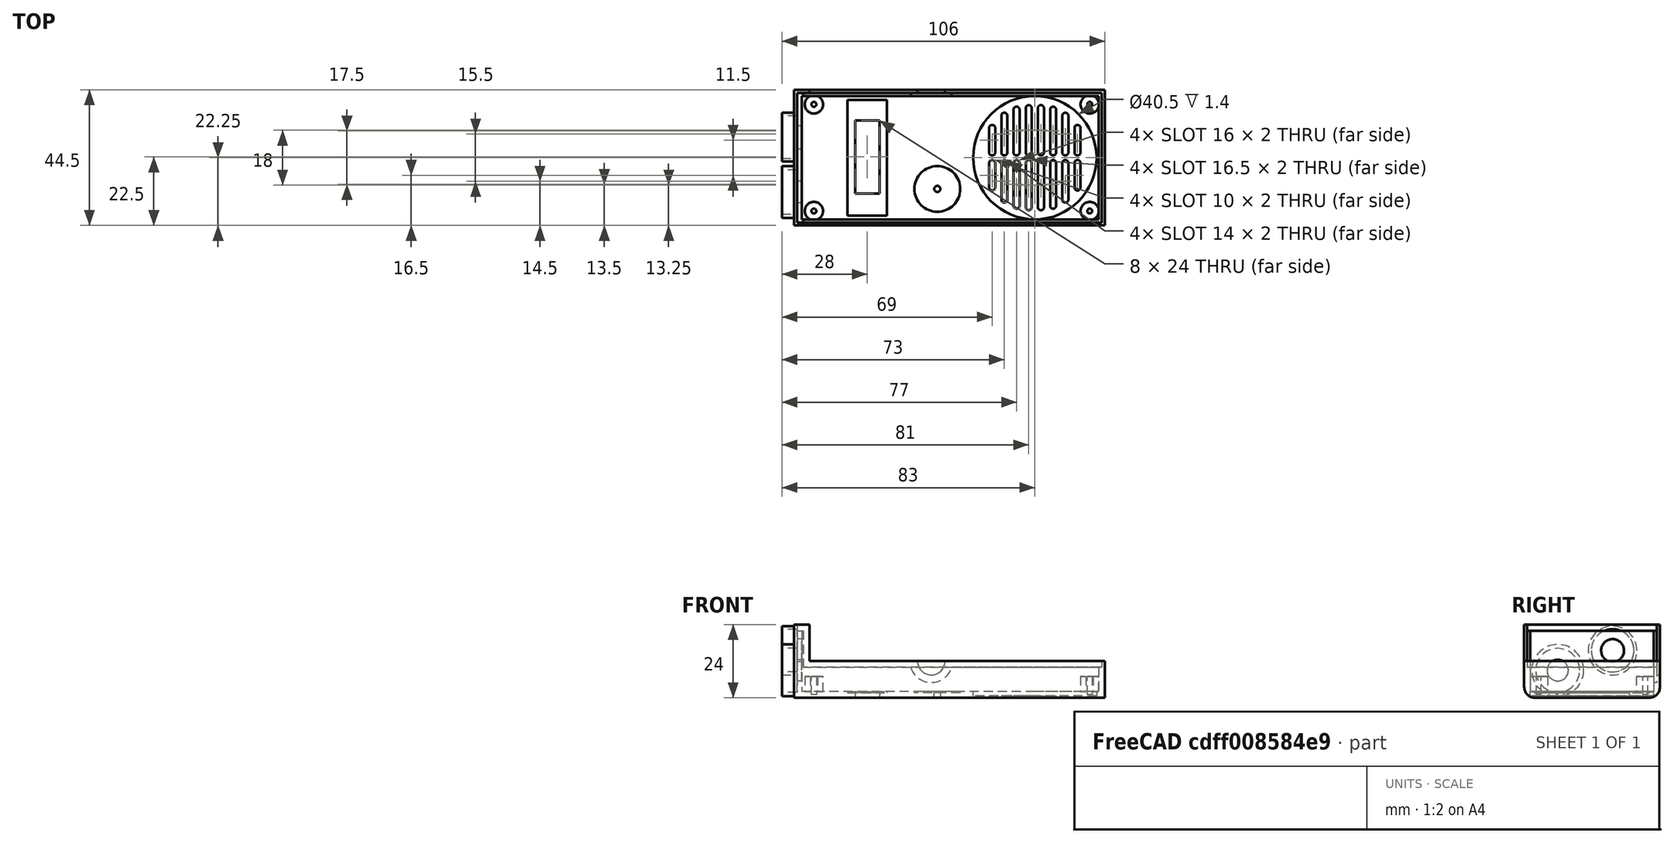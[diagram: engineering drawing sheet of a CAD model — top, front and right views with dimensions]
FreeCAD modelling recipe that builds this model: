
FCSTD DOCUMENT  (FreeCAD 0.20R)
Label: base
License: All rights reserved
LicenseURL: http://en.wikipedia.org/wiki/All_rights_reserved
objects: Sketcher::SketchObject×17, PartDesign::Pocket×14, PartDesign::Pad×3, PartDesign::Plane×2, PartDesign::Mirrored×2, PartDesign::Fillet×1, PartDesign::MultiTransform×1, PartDesign::Body×1
note: 59 computed .brp shape members not serialized (recipe doc carries the construction recipe); baked Part::Feature solids carry a one-line shape summary decoded from their .brp

FEATURE [Sketcher::SketchObject] Sketch  label="sketch_foundation"
  FullyConstrained = true
  MapMode = 5
  Support = -> [XY_Plane]
  sketch-geometry (4):
    g0: LineSegment StartX=0 StartY=0 StartZ=0 EndX=102 EndY=0 EndZ=0
    g1: LineSegment StartX=102 StartY=0 StartZ=0 EndX=102 EndY=44.5 EndZ=0
    g2: LineSegment StartX=102 StartY=44.5 StartZ=0 EndX=0 EndY=44.5 EndZ=0
    g3: LineSegment StartX=0 StartY=44.5 StartZ=0 EndX=0 EndY=0 EndZ=0
  constraints (11):
    c: Coincident(g0,g1)
    c: Coincident(g1,g2)
    c: Coincident(g2,g3)
    c: Coincident(g3,g0)
    c: Horizontal(g0)
    c: Horizontal(g2)
    c: Vertical(g1)
    c: Vertical(g3)
    c: Coincident(g0,g-1)
    c: Distance(g3) = 44.5
    c: Distance(g2) = 102
FEATURE [PartDesign::Pad] Pad  label="pad_foundation"
  Direction = (0,0,1)
  Length = 24
  Length2 = 10
  Profile = -> Sketch
  ReferenceAxis = -> Sketch [N_Axis]
  Type = 0
FEATURE [Sketcher::SketchObject] Sketch001  label="sketch_pocket_foundation"
  FullyConstrained = true
  MapMode = 5
  Placement = pos=(0,0,24) rot=(0,0,1;0rad)
  Support = -> [Pad]
  sketch-geometry (4):
    g0: LineSegment StartX=2.5 StartY=42.5 StartZ=0 EndX=100 EndY=42.5 EndZ=0
    g1: LineSegment StartX=100 StartY=42.5 StartZ=0 EndX=100 EndY=2 EndZ=0
    g2: LineSegment StartX=100 StartY=2 StartZ=0 EndX=2.5 EndY=2 EndZ=0
    g3: LineSegment StartX=2.5 StartY=2 StartZ=0 EndX=2.5 EndY=42.5 EndZ=0
  constraints (12):
    c: Coincident(g0,g1)
    c: Coincident(g1,g2)
    c: Coincident(g2,g3)
    c: Coincident(g3,g0)
    c: Horizontal(g0)
    c: Horizontal(g2)
    c: Vertical(g1)
    c: Vertical(g3)
    c: DistanceY(g-1,g2) = 2
    c: DistanceX(g-2,g2) = 2.5
    c: Distance(g1) = 40.5
    c: Distance(g0) = 97.5
FEATURE [PartDesign::Pocket] Pocket  label="pocket_foundation"
  BaseFeature = -> Pad
  Direction = (0,0,-1)
  Length = 22
  Length2 = 5
  Profile = -> Sketch001
  ReferenceAxis = -> Sketch001 [N_Axis]
  Type = 0
FEATURE [Sketcher::SketchObject] Sketch002  label="sketch_pocket_split"
  FullyConstrained = true
  MapMode = 5
  Placement = pos=(0,0,24) rot=(0,0,1;0rad)
  Support = -> [Pocket]
  sketch-geometry (4):
    g0: LineSegment StartX=5 StartY=44.5 StartZ=0 EndX=102 EndY=44.5 EndZ=0
    g1: LineSegment StartX=102 StartY=44.5 StartZ=0 EndX=102 EndY=0 EndZ=0
    g2: LineSegment StartX=102 StartY=0 StartZ=0 EndX=5 EndY=0 EndZ=0
    g3: LineSegment StartX=5 StartY=0 StartZ=0 EndX=5 EndY=44.5 EndZ=0
  constraints (12):
    c: Coincident(g0,g1)
    c: Coincident(g1,g2)
    c: Coincident(g2,g3)
    c: Coincident(g3,g0)
    c: Horizontal(g0)
    c: Horizontal(g2)
    c: Vertical(g1)
    c: Vertical(g3)
    c: PointOnObject(g1,g-1)
    c: DistanceX(g-2,g2) = 5
    c: Distance(g2) = 97
    c: Distance(g1) = 44.5
FEATURE [PartDesign::Pocket] Pocket001  label="pocket_split"
  BaseFeature = -> Pocket
  Direction = (0,0,-1)
  Length = 12
  Length2 = 5
  Profile = -> Sketch002
  ReferenceAxis = -> Sketch002 [N_Axis]
  Type = 0
FEATURE [Sketcher::SketchObject] Sketch003  label="sketch_board_stand"
  FullyConstrained = true
  MapMode = 5
  Placement = pos=(0,0,2) rot=(0,0,1;0rad)
  Support = -> [Pocket001]
  sketch-geometry (4):
    g0: Circle CenterX=6.5 CenterY=39.75 CenterZ=0 NormalX=0 NormalY=0 NormalZ=1 AngleXU=0 Radius=3
    g1: Circle CenterX=97 CenterY=39.75 CenterZ=0 NormalX=0 NormalY=0 NormalZ=1 AngleXU=0 Radius=3
    g2: Circle CenterX=6.5 CenterY=4.75 CenterZ=0 NormalX=0 NormalY=0 NormalZ=1 AngleXU=0 Radius=3
    g3: Circle CenterX=97 CenterY=4.75 CenterZ=0 NormalX=0 NormalY=0 NormalZ=1 AngleXU=0 Radius=3
  constraints (12):
    c: Equal(g0,g1)
    c: Equal(g1,g2)
    c: Equal(g2,g3)
    c: Distance(g0,g1) = 90.5
    c: Distance(g2,g3) = 90.5
    c: Distance(g1,g3) = 35
    c: Distance(g2,g0) = 35
    c: Diameter(g1) = 6
    c: DistanceX(g-2,g1) = 97
    c: DistanceX(g-2,g3) = 97
    c: DistanceY(g-1,g3) = 4.75
    c: DistanceY(g-1,g2) = 4.75
FEATURE [PartDesign::Pad] Pad001  label="pad_board_stand"
  BaseFeature = -> Pocket001
  Direction = (0,0,1)
  Length = 5
  Length2 = 10
  Profile = -> Sketch003
  ReferenceAxis = -> Sketch003 [N_Axis]
  Type = 0
FEATURE [Sketcher::SketchObject] Sketch004  label="sketch_pocket_inner_face"
  FullyConstrained = true
  MapMode = 5
  Placement = pos=(0,0,2) rot=(0,0,1;0rad)
  Support = -> [Pad001]
  sketch-geometry (5):
    g0: Circle CenterX=47 CenterY=12 CenterZ=0 NormalX=0 NormalY=0 NormalZ=1 AngleXU=0 Radius=7.5
    g1: LineSegment StartX=17.5 StartY=41.25 StartZ=0 EndX=30.5 EndY=41.25 EndZ=0
    g2: LineSegment StartX=30.5 StartY=41.25 StartZ=0 EndX=30.5 EndY=3.25 EndZ=0
    g3: LineSegment StartX=30.5 StartY=3.25 StartZ=0 EndX=17.5 EndY=3.25 EndZ=0
    g4: LineSegment StartX=17.5 StartY=3.25 StartZ=0 EndX=17.5 EndY=41.25 EndZ=0
  constraints (15):
    c: Diameter(g0) = 15
    c: DistanceY(g-1,g0) = 12
    c: DistanceX(g-2,g0) = 47
    c: Coincident(g1,g2)
    c: Coincident(g2,g3)
    c: Coincident(g3,g4)
    c: Coincident(g4,g1)
    c: Horizontal(g1)
    c: Horizontal(g3)
    c: Vertical(g2)
    c: Vertical(g4)
    c: Distance(g2) = 38
    c: Distance(g3) = 13
    c: DistanceY(g-1,g3) = 3.25
    c: DistanceX(g-2,g1) = 17.5
FEATURE [PartDesign::Pocket] Pocket002  label="pocket_inner_face"
  BaseFeature = -> Pad001
  Direction = (0,0,-1)
  Length = 0.4
  Length2 = 5
  Profile = -> Sketch004
  ReferenceAxis = -> Sketch004 [N_Axis]
  Type = 0
FEATURE [Sketcher::SketchObject] Sketch005  label="sketch_screen_hole"
  FullyConstrained = true
  MapMode = 5
  Placement = pos=(0,0,1.6) rot=(0,0,1;0rad)
  Support = -> [Pocket002]
  sketch-geometry (4):
    g0: LineSegment StartX=20 StartY=34.5 StartZ=0 EndX=28 EndY=34.5 EndZ=0
    g1: LineSegment StartX=28 StartY=34.5 StartZ=0 EndX=28 EndY=10.5 EndZ=0
    g2: LineSegment StartX=28 StartY=10.5 StartZ=0 EndX=20 EndY=10.5 EndZ=0
    g3: LineSegment StartX=20 StartY=10.5 StartZ=0 EndX=20 EndY=34.5 EndZ=0
  constraints (12):
    c: Coincident(g0,g1)
    c: Coincident(g1,g2)
    c: Coincident(g2,g3)
    c: Coincident(g3,g0)
    c: Horizontal(g0)
    c: Horizontal(g2)
    c: Vertical(g1)
    c: Vertical(g3)
    c: Distance(g0) = 8
    c: Distance(g1) = 24
    c: DistanceX(g-2,g2) = 20
    c: DistanceY(g-1,g2) = 10.5
FEATURE [PartDesign::Pocket] Pocket003  label="pocket_screen_hole"
  BaseFeature = -> Pocket002
  Direction = (0,0,-1)
  Length = 5
  Length2 = 5
  Profile = -> Sketch005
  ReferenceAxis = -> Sketch005 [N_Axis]
  Type = 0
FEATURE [Sketcher::SketchObject] Sketch006  label="sketch_stand_holes"
  FullyConstrained = true
  MapMode = 5
  Placement = pos=(0,0,7) rot=(0,0,1;0rad)
  Support = -> [Pocket003]
  sketch-geometry (4):
    g0: Circle CenterX=6.5 CenterY=39.75 CenterZ=0 NormalX=0 NormalY=0 NormalZ=1 AngleXU=0 Radius=0.8
    g1: Circle CenterX=97 CenterY=39.75 CenterZ=0 NormalX=0 NormalY=0 NormalZ=1 AngleXU=0 Radius=0.8
    g2: Circle CenterX=6.5 CenterY=4.75 CenterZ=0 NormalX=0 NormalY=0 NormalZ=1 AngleXU=0 Radius=0.8
    g3: Circle CenterX=97 CenterY=4.75 CenterZ=0 NormalX=0 NormalY=0 NormalZ=1 AngleXU=0 Radius=0.8
  constraints (12):
    c: Equal(g0,g1)
    c: Equal(g1,g3)
    c: Equal(g3,g2)
    c: Diameter(g0) = 1.6
    c: Distance(g0,g1) = 90.5
    c: Distance(g2,g3) = 90.5
    c: Distance(g3,g1) = 35
    c: Distance(g0,g2) = 35
    c: DistanceY(g-1,g3) = 4.75
    c: DistanceY(g-1,g2) = 4.75
    c: DistanceX(g-2,g0) = 6.5
    c: DistanceX(g-2,g2) = 6.5
FEATURE [PartDesign::Pocket] Pocket004  label="pocket_stand_holes"
  BaseFeature = -> Pocket003
  Direction = (0,0,-1)
  Length = 6
  Length2 = 5
  Profile = -> Sketch006
  ReferenceAxis = -> Sketch006 [N_Axis]
  Type = 0
FEATURE [Sketcher::SketchObject] Sketch007  label="sketch_mic_hole"
  FullyConstrained = true
  MapMode = 5
  Placement = pos=(0,0,2) rot=(0,0,1;0rad)
  Support = -> [Pocket004]
  sketch-geometry (1):
    g0: Circle CenterX=47 CenterY=12 CenterZ=0 NormalX=0 NormalY=0 NormalZ=1 AngleXU=0 Radius=1
  constraints (3):
    c: Diameter(g0) = 2
    c: DistanceY(g-1,g0) = 12
    c: DistanceX(g-2,g0) = 47
FEATURE [PartDesign::Pocket] Pocket005  label="pocket_mic_hole"
  BaseFeature = -> Pocket004
  Direction = (0,0,-1)
  Length = 5
  Length2 = 5
  Profile = -> Sketch007
  ReferenceAxis = -> Sketch007 [N_Axis]
  Type = 0
FEATURE [Sketcher::SketchObject] Sketch009  label="sketch_ptt_hole"
  FullyConstrained = true
  MapMode = 5
  Placement = pos=(0,44.5,0) rot=(0,0.707107,0.707107;3.14159rad)
  Support = -> [Pocket005]
  sketch-geometry (1):
    g0: Circle CenterX=-45 CenterY=12 CenterZ=0 NormalX=0 NormalY=0 NormalZ=1 AngleXU=0 Radius=4.5
  constraints (3):
    c: Diameter(g0) = 9
    c: DistanceY(g-1,g0) = 12
    c: DistanceX(g-2,g0) = -45
FEATURE [PartDesign::Pocket] Pocket007  label="pocket_ptt_hole"
  BaseFeature = -> Pocket005
  Direction = (0,-1,2e-16)
  Length = 5
  Length2 = 5
  Profile = -> Sketch009
  ReferenceAxis = -> Sketch009 [N_Axis]
  Type = 0
FEATURE [Sketcher::SketchObject] Sketch010  label="sketch_antenna_rotary_pad"
  FullyConstrained = true
  MapMode = 5
  Placement = pos=(0,0,0) rot=(0.57735,-0.57735,-0.57735;2.0944rad)
  Support = -> [Pocket007]
  sketch-geometry (2):
    g0: Circle CenterX=-11 CenterY=9 CenterZ=0 NormalX=0 NormalY=0 NormalZ=1 AngleXU=0 Radius=8.5
    g1: Circle CenterX=-29 CenterY=15.5 CenterZ=0 NormalX=0 NormalY=0 NormalZ=1 AngleXU=0 Radius=8
  constraints (6):
    c: Diameter(g0) = 17
    c: DistanceX(g-2,g0) = -11
    c: DistanceY(g-1,g0) = 9
    c: Diameter(g1) = 16
    c: DistanceX(g-2,g1) = -29
    c: DistanceY(g-1,g1) = 15.5
FEATURE [PartDesign::Pad] Pad002  label="pad_antenna_rotary"
  BaseFeature = -> Pocket007
  Direction = (-1,0,0)
  Length = 4
  Length2 = 10
  Profile = -> Sketch010
  ReferenceAxis = -> Sketch010 [N_Axis]
  Type = 0
FEATURE [Sketcher::SketchObject] Sketch011  label="sketch_antenna_rotary_pocket"
  FullyConstrained = true
  MapMode = 5
  Placement = pos=(-4,0,0) rot=(0.57735,-0.57735,-0.57735;2.0944rad)
  Support = -> [Pad002]
  sketch-geometry (2):
    g0: Circle CenterX=-11 CenterY=9 CenterZ=0 NormalX=0 NormalY=0 NormalZ=1 AngleXU=0 Radius=7.2
    g1: Circle CenterX=-29 CenterY=15.5 CenterZ=0 NormalX=0 NormalY=0 NormalZ=1 AngleXU=0 Radius=7
  constraints (6):
    c: Diameter(g0) = 14.4
    c: DistanceX(g-2,g0) = -11
    c: DistanceY(g-1,g0) = 9
    c: Diameter(g1) = 14
    c: DistanceX(g-2,g1) = -29
    c: DistanceY(g-1,g1) = 15.5
FEATURE [PartDesign::Pocket] Pocket008  label="pocket_antenna_rotary"
  BaseFeature = -> Pad002
  Direction = (1,0,0)
  Length = 5
  Length2 = 5
  Profile = -> Sketch011
  ReferenceAxis = -> Sketch011 [N_Axis]
  Type = 0
FEATURE [Sketcher::SketchObject] Sketch012  label="sketch_antenna_rotary_hole"
  FullyConstrained = true
  MapMode = 5
  Placement = pos=(0,0,0) rot=(0.57735,-0.57735,-0.57735;2.0944rad)
  Support = -> [Pocket008]
  sketch-geometry (2):
    g0: Circle CenterX=-11 CenterY=9 CenterZ=0 NormalX=0 NormalY=0 NormalZ=1 AngleXU=0 Radius=3.5
    g1: Circle CenterX=-29 CenterY=15.5 CenterZ=0 NormalX=0 NormalY=0 NormalZ=1 AngleXU=0 Radius=3.75
  constraints (6):
    c: Diameter(g0) = 7
    c: DistanceX(g-2,g0) = -11
    c: DistanceY(g-1,g0) = 9
    c: Diameter(g1) = 7.5
    c: DistanceY(g-1,g1) = 15.5
    c: DistanceX(g-2,g1) = -29
FEATURE [PartDesign::Pocket] Pocket009  label="pocket_antenna_rotary_hole"
  BaseFeature = -> Pocket008
  Direction = (1,0,0)
  Length = 10
  Length2 = 5
  Profile = -> Sketch012
  ReferenceAxis = -> Sketch012 [N_Axis]
  Type = 0
FEATURE [Sketcher::SketchObject] Sketch013  label="sketch_insertion_pocket"
  FullyConstrained = true
  MapMode = 5
  Placement = pos=(0,0,24) rot=(0,0,1;0rad)
  Support = -> [Pocket009]
  sketch-geometry (4):
    g0: LineSegment StartX=3 StartY=43.5 StartZ=0 EndX=101 EndY=43.5 EndZ=0
    g1: LineSegment StartX=101 StartY=43.5 StartZ=0 EndX=101 EndY=1 EndZ=0
    g2: LineSegment StartX=101 StartY=1 StartZ=0 EndX=3 EndY=1 EndZ=0
    g3: LineSegment StartX=3 StartY=1 StartZ=0 EndX=3 EndY=43.5 EndZ=0
  constraints (12):
    c: Coincident(g0,g1)
    c: Coincident(g1,g2)
    c: Coincident(g2,g3)
    c: Coincident(g3,g0)
    c: Horizontal(g0)
    c: Horizontal(g2)
    c: Vertical(g1)
    c: Vertical(g3)
    c: DistanceY(g-1,g2) = 1
    c: Distance(g2) = 98
    c: Distance(g1) = 42.5
    c: DistanceX(g-2,g0) = 3
FEATURE [PartDesign::Pocket] Pocket010  label="pocket_insertion"
  BaseFeature = -> Pocket009
  Direction = (0,0,-1)
  Length = 14
  Length2 = 5
  Profile = -> Sketch013
  ReferenceAxis = -> Sketch013 [N_Axis]
  Type = 0
FEATURE [Sketcher::SketchObject] Sketch014  label="sketch_insertion_pocket_small"
  FullyConstrained = true
  MapMode = 5
  Placement = pos=(0,0,24) rot=(0,0,1;0rad)
  Support = -> [Pocket010]
  sketch-geometry (4):
    g0: LineSegment StartX=1 StartY=43.5 StartZ=0 EndX=5 EndY=43.5 EndZ=0
    g1: LineSegment StartX=5 StartY=43.5 StartZ=0 EndX=5 EndY=1 EndZ=0
    g2: LineSegment StartX=5 StartY=1 StartZ=0 EndX=1 EndY=1 EndZ=0
    g3: LineSegment StartX=1 StartY=1 StartZ=0 EndX=1 EndY=43.5 EndZ=0
  constraints (12):
    c: Coincident(g0,g1)
    c: Coincident(g1,g2)
    c: Coincident(g2,g3)
    c: Coincident(g3,g0)
    c: Horizontal(g0)
    c: Horizontal(g2)
    c: Vertical(g1)
    c: Vertical(g3)
    c: DistanceX(g-2,g0) = 1
    c: DistanceY(g-1,g2) = 1
    c: Distance(g2) = 4
    c: Distance(g3) = 42.5
FEATURE [PartDesign::Pocket] Pocket011  label="pocket_insertion_small"
  BaseFeature = -> Pocket010
  Direction = (0,0,-1)
  Length = 2
  Length2 = 5
  Profile = -> Sketch014
  ReferenceAxis = -> Sketch014 [N_Axis]
  Type = 0
FEATURE [Sketcher::SketchObject] Sketch015  label="sketch_ptt_inner_pocket"
  FullyConstrained = true
  MapMode = 5
  Placement = pos=(0,42.5,0) rot=(1,0,0;1.5708rad)
  sketch-geometry (1):
    g0: Circle CenterX=45 CenterY=12 CenterZ=0 NormalX=0 NormalY=0 NormalZ=1 AngleXU=0 Radius=7
  constraints (3):
    c: Diameter(g0) = 14
    c: DistanceX(g-2,g0) = 45
    c: DistanceY(g-1,g0) = 12
FEATURE [PartDesign::Pocket] Pocket012  label="pocket_btt_inner"
  BaseFeature = -> Pocket011
  Direction = (0,1,-2e-16)
  Length = 1
  Length2 = 5
  Profile = -> Sketch015
  ReferenceAxis = -> Sketch015 [N_Axis]
  Type = 0
FEATURE [Sketcher::SketchObject] Sketch020  label="sketch_speaker_pocket"
  FullyConstrained = true
  MapMode = 5
  Placement = pos=(0,0,2) rot=(0,0,1;0rad)
  Support = -> [Pocket012]
  sketch-geometry (1):
    g0: Circle CenterX=79 CenterY=22.25 CenterZ=0 NormalX=0 NormalY=0 NormalZ=1 AngleXU=0 Radius=20.25
  constraints (3):
    c: Diameter(g0) = 40.5
    c: DistanceY(g-1,g0) = 22.25
    c: DistanceX(g-2,g0) = 79
FEATURE [PartDesign::Pocket] Pocket017  label="pocket_speaker"
  BaseFeature = -> Pocket012
  Direction = (0,0,-1)
  Length = 1.4
  Length2 = 5
  Profile = -> Sketch020
  ReferenceAxis = -> Sketch020 [N_Axis]
  Type = 0
FEATURE [PartDesign::Fillet] Fillet  label="fillet_main"
  Base = -> Pocket017 [Edge1,Edge9]
  BaseFeature = -> Pocket017
  Radius = 3.5
  SupportTransform = false
  UseAllEdges = false
FEATURE [Sketcher::SketchObject] Sketch021  label="sketch_pocket_speaker_base"
  FullyConstrained = true
  MapMode = 5
  Placement = pos=(0,0,0.6) rot=(0,0,1;0rad)
  Support = -> [Fillet]
  sketch-geometry (16):
    g0: ArcOfCircle CenterX=77 CenterY=38.5 CenterZ=0 NormalX=0 NormalY=0 NormalZ=1 AngleXU=0 Radius=1 StartAngle=0 EndAngle=3.14159
    g1: ArcOfCircle CenterX=77 CenterY=24 CenterZ=0 NormalX=0 NormalY=0 NormalZ=1 AngleXU=0 Radius=1 StartAngle=3.14159 EndAngle=6.28319
    g2: LineSegment StartX=76 StartY=38.5 StartZ=0 EndX=76 EndY=24 EndZ=0
    g3: LineSegment StartX=78 StartY=24 StartZ=0 EndX=78 EndY=38.5 EndZ=0
    g4: ArcOfCircle CenterX=73 CenterY=38 CenterZ=0 NormalX=0 NormalY=0 NormalZ=1 AngleXU=0 Radius=1 StartAngle=-9e-16 EndAngle=3.14159
    g5: ArcOfCircle CenterX=73 CenterY=24 CenterZ=0 NormalX=0 NormalY=0 NormalZ=1 AngleXU=0 Radius=1 StartAngle=3.14159 EndAngle=6.28319
    g6: LineSegment StartX=72 StartY=38 StartZ=0 EndX=72 EndY=24 EndZ=0
    g7: LineSegment StartX=74 StartY=24 StartZ=0 EndX=74 EndY=38 EndZ=0
    g8: ArcOfCircle CenterX=69 CenterY=36 CenterZ=0 NormalX=0 NormalY=0 NormalZ=1 AngleXU=0 Radius=1 StartAngle=-2.7e-15 EndAngle=3.14159
    g9: ArcOfCircle CenterX=69 CenterY=24 CenterZ=0 NormalX=0 NormalY=0 NormalZ=1 AngleXU=0 Radius=1 StartAngle=3.14159 EndAngle=6.28319
    g10: LineSegment StartX=68 StartY=36 StartZ=0 EndX=68 EndY=24 EndZ=0
    g11: LineSegment StartX=70 StartY=24 StartZ=0 EndX=70 EndY=36 EndZ=0
    g12: ArcOfCircle CenterX=65 CenterY=32 CenterZ=0 NormalX=0 NormalY=0 NormalZ=1 AngleXU=0 Radius=1 StartAngle=-1.8e-15 EndAngle=3.14159
    g13: ArcOfCircle CenterX=65 CenterY=24 CenterZ=0 NormalX=0 NormalY=0 NormalZ=1 AngleXU=0 Radius=1 StartAngle=3.14159 EndAngle=6.28319
    g14: LineSegment StartX=64 StartY=32 StartZ=0 EndX=64 EndY=24 EndZ=0
    g15: LineSegment StartX=66 StartY=24 StartZ=0 EndX=66 EndY=32 EndZ=0
  constraints (40):
    c: Tangent(g0,g2) = -1.5708
    c: Tangent(g2,g1) = -1.5708
    c: Tangent(g1,g3) = -1.5708
    c: Tangent(g3,g0) = -1.5708
    c: Equal(g0,g1)
    c: Vertical(g2)
    c: Radius(g1) = 1
    c: Tangent(g4,g6) = -1.5708
    c: Tangent(g6,g5) = -1.5708
    c: Tangent(g5,g7) = -1.5708
    c: Tangent(g7,g4) = -1.5708
    c: Equal(g4,g5)
    c: Vertical(g6)
    c: Tangent(g8,g10) = -1.5708
    c: Tangent(g10,g9) = -1.5708
    c: Tangent(g9,g11) = -1.5708
    c: Tangent(g11,g8) = -1.5708
    c: Equal(g8,g9)
    c: Vertical(g10)
    c: Tangent(g12,g14) = -1.5708
    c: Tangent(g14,g13) = -1.5708
    c: Tangent(g13,g15) = -1.5708
    c: Tangent(g15,g12) = -1.5708
    c: Equal(g12,g13)
    c: Vertical(g14)
    c: Equal(g1,g5)
    c: Equal(g5,g9)
    c: Equal(g9,g13)
    c: Distance(g12,g10) = 2
    c: Distance(g8,g6) = 2
    c: Distance(g4,g2) = 2
    c: DistanceY(g-1,g13) = 24
    c: DistanceY(g-1,g9) = 24
    c: DistanceY(g-1,g5) = 24
    c: DistanceY(g-1,g1) = 24
    c: DistanceX(g-2,g1) = 77
    c: Distance(g14) = 8
    c: Distance(g10) = 12
    c: Distance(g6) = 14
    c: Distance(g2) = 14.5
FEATURE [PartDesign::Pocket] Pocket018  label="pocket_speaker_base"
  BaseFeature = -> Fillet
  Direction = (0,0,-1)
  Length = 5
  Length2 = 5
  Profile = -> Sketch021
  ReferenceAxis = -> Sketch021 [N_Axis]
  Type = 0
FEATURE [PartDesign::Plane] DatumPlane  label="datum_plane_vertical_speaker"
  AttachmentOffset = pos=(0,0,79) rot=(0,0,1;0rad)
  Length = 81.2898
  MapMode = 4
  Placement = pos=(79,0,0) rot=(0.57735,0.57735,0.57735;2.0944rad)
  ResizeMode = 0
  Support = -> [Pocket018]
  Width = 61.7898
FEATURE [PartDesign::Plane] DatumPlane001  label="datum_plane_horizontal_speaker"
  AttachmentOffset = pos=(0,0,-22.25) rot=(0,0,1;0rad)
  Length = 142.937
  MapMode = 5
  Placement = pos=(0,22.25,4.9e-15) rot=(1,0,0;1.5708rad)
  ResizeMode = 0
  Support = -> [XZ_Plane]
  Width = 65.9374
FEATURE [PartDesign::Mirrored] Mirrored
  MirrorPlane = -> DatumPlane
FEATURE [PartDesign::Mirrored] Mirrored001
  MirrorPlane = -> DatumPlane001
FEATURE [PartDesign::MultiTransform] MultiTransform  label="multi_transform_speaker"
  BaseFeature = -> Pocket018
  Originals = -> [Pocket018]
  Transformations = -> [Mirrored,Mirrored001]
FEATURE [PartDesign::Body] Body
  Group = -> [Sketch,Pad,Sketch001,Pocket,Sketch002,Pocket001,Sketch003,Pad001,Sketch004,Pocket002,Sketch005,Pocket003,Sketch006,Pocket004,Sketch007,Pocket005,Sketch009,Pocket007,Sketch010,Pad002,Sketch011,Pocket008,Sketch012,Pocket009,Sketch013,Pocket010,Sketch014,Pocket011,Sketch015,Pocket012,Sketch020,Pocket017,Fillet,Sketch021,Pocket018,DatumPlane,DatumPlane001,MultiTransform,Mirrored,Mirrored001]
  Origin = -> Origin
  Tip = -> MultiTransform
